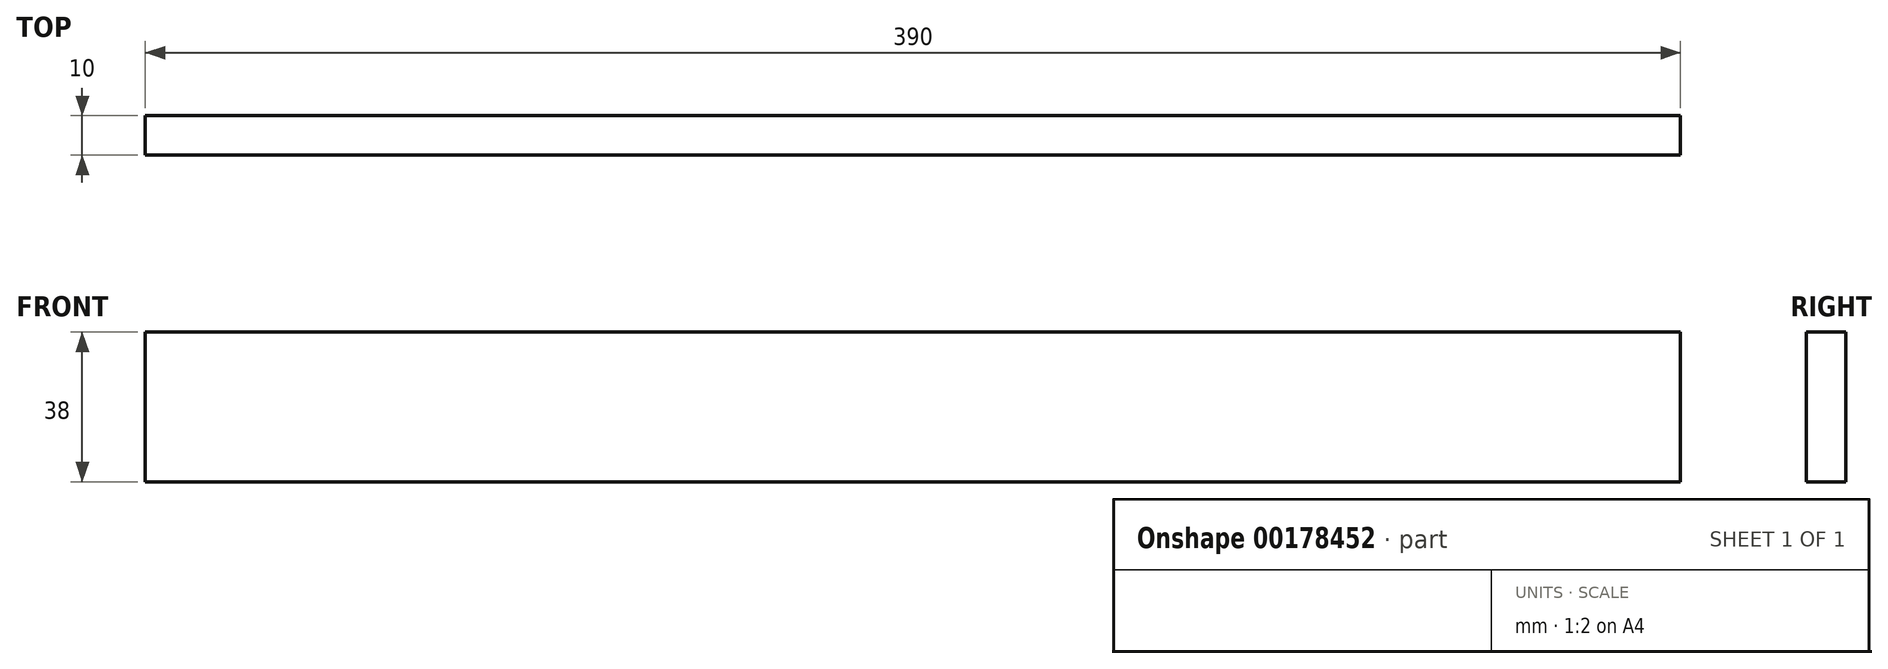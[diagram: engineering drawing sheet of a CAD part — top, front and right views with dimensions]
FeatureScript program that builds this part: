
annotation { "Feature Type Name" : "Feature", "Feature Type Description" : "" }
export const myFeature = defineFeature(function(context is Context, id is Id, definition is map)
    precondition{}
    {
        {
            var Q0;
            Q0=qCreatedBy(makeId("Front.planeOp"),FACE);
            var sketch = newSketch(context, id + "F0", { "sketchPlane" : qUnion([Q0])});
            skLineSegment(sketch, "E0.bottom", {"start": v(0, 0) * mm, "end": v(390, 0) * mm});
            skLineSegment(sketch, "E0.top", {"start": v(0, 38) * mm, "end": v(390, 38) * mm});
            skLineSegment(sketch, "E0.left", {"start": v(0, 0) * mm, "end": v(0, 38) * mm});
            skLineSegment(sketch, "E0.right", {"start": v(390, 0) * mm, "end": v(390, 38) * mm});
            skSolve(sketch);
        }
        {
            var Q0;
            Q0=qSketchRegion(id+"F0",true);
            extrude(context, id + "F1", {"entities" : qUnion([Q0]), "depth" : 10 * mm});
        }
    });
